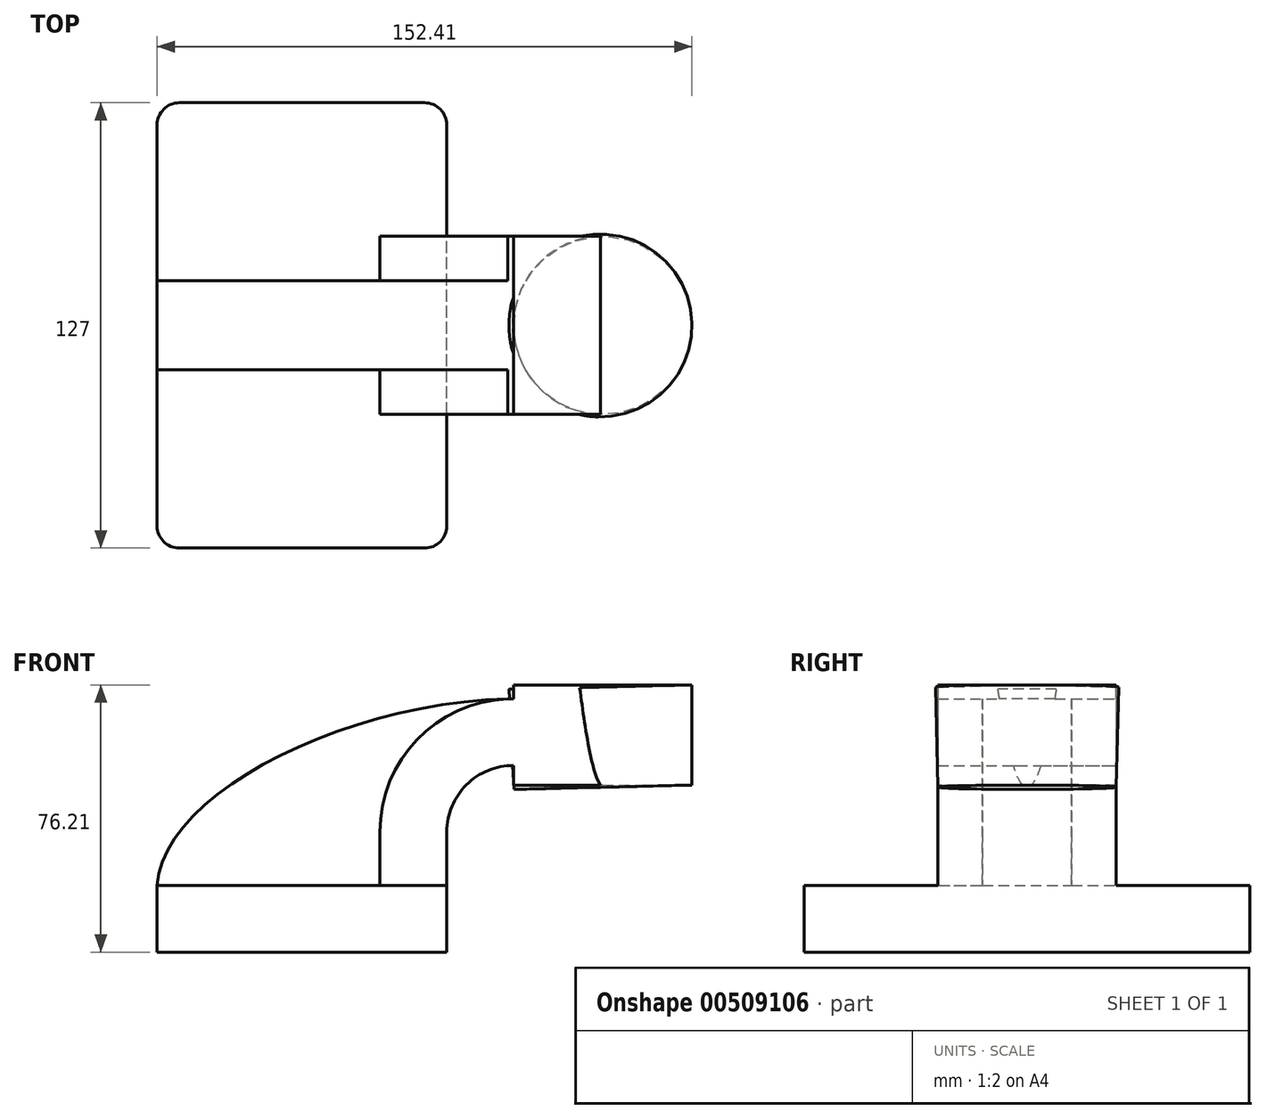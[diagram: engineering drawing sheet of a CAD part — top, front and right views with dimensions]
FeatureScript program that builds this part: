
annotation { "Feature Type Name" : "Feature", "Feature Type Description" : "" }
export const myFeature = defineFeature(function(context is Context, id is Id, definition is map)
    precondition{}
    {
        {
            var Q0;
            Q0=qCreatedBy(makeId("Front.planeOp"),FACE);
            var sketch = newSketch(context, id + "F0", { "sketchPlane" : qUnion([Q0])});
            skLineSegment(sketch, "E0.bottom", {"start": v(-41.28, 9.52) * mm, "end": v(41.28, 9.53) * mm});
            skLineSegment(sketch, "E0.top", {"start": v(-41.28, -9.53) * mm, "end": v(41.28, -9.53) * mm});
            skLineSegment(sketch, "E0.left", {"start": v(-41.28, 9.52) * mm, "end": v(-41.28, -9.53) * mm});
            skLineSegment(sketch, "E0.right", {"start": v(41.28, 9.53) * mm, "end": v(41.28, -9.52) * mm});
            skPoint(sketch, "E0.middle", {"position": v(0, 0) * mm});
            skLineSegment(sketch, "E1.bottom", {"start": v(60.32, 38.1) * mm, "end": v(111.12, 38.1) * mm});
            skLineSegment(sketch, "E1.top", {"start": v(60.32, 66.68) * mm, "end": v(111.12, 66.68) * mm});
            skLineSegment(sketch, "E1.left", {"start": v(60.32, 38.1) * mm, "end": v(60.32, 66.68) * mm});
            skLineSegment(sketch, "E1.right", {"start": v(111.12, 38.1) * mm, "end": v(111.12, 66.68) * mm});
            skPoint(sketch, "E1.middle", {"position": v(85.72, 52.39) * mm});
            skPoint(sketch, "E2.endSnap0", {"position": v(85.72, 38.1) * mm});
            skLineSegment(sketch, "E3", {"start": v(41.28, 9.53) * mm, "end": v(41.28, 24.77) * mm});
            skArc(sketch, "E4", {"start": v(41.27, 24.77) * mm, "mid": v(46.86, 38.19) * mm, "end": v(60.32, 43.67) * mm});
            skLineSegment(sketch, "E5", {"start": v(60.32, 43.67) * mm, "end": v(85.72, 43.67) * mm});
            skArc(sketch, "E6.0", {"start": v(22.23, 24.77) * mm, "mid": v(33.4, 51.66) * mm, "end": v(60.32, 62.72) * mm});
            skLineSegment(sketch, "E7", {"start": v(22.23, 24.77) * mm, "end": v(22.23, 9.53) * mm});
            skLineSegment(sketch, "E8", {"start": v(60.32, 62.72) * mm, "end": v(85.03, 62.72) * mm});
            skLineSegment(sketch, "E9", {"start": v(85.72, 38.1) * mm, "end": v(85.03, 66.68) * mm});
            skFitSpline(sketch, "E10", {"points": [v(-41.28, 9.52) * mm, v(60.32, 62.72) * mm], "startDerivative": vector(4.2, 78.01) * mm, "endDerivative": vector(143.8, 1.78) * mm});
            skSolve(sketch);
        }
        {
            var Q0;
            Q0=makeQuery(id+"F0.imprint","IMPRINT",FACE,{"disambiguationData":[TD([[makeQuery(id+"F0.imprint","IMPRINT",EDGE,{"derivedFrom":sQuery(id+"F0.wireOp",EDGE,"E0.top")}),1.0]])]});
            extrude(context, id + "F1", {"entities" : qUnion([Q0]), "endBound" : BoundingType.SYMMETRIC, "depth" : 127 * mm});
        }
        {
            var Q0;
            {var subQ1=sQuery(id+"F0.wireOp",EDGE,"E3");Q0=makeQuery(id+"F0.imprint","IMPRINT",FACE,{"disambiguationData":[TD([[makeQuery(id+"F0.imprint","IMPRINT",EDGE,{"derivedFrom":subQ1}),1.0]])]});}
            var Q1;
            {var subQ0=sQuery(id+"F0.wireOp",EDGE,"E1.left");var subQ1=sQuery(id+"F0.wireOp",EDGE,"E1.top");var subQ2=makeQuery(id+"F0.imprint","INTERSECT",VERTEX,{"derivedFrom":[subQ1,subQ0]});Q1=makeQuery(id+"F0.imprint","IMPRINT",FACE,{"disambiguationData":[TD([[makeQuery(id+"F0.imprint","IMPRINT",EDGE,{"disambiguationData":[TD([[subQ2,-1.0]])],"derivedFrom":subQ1}),-1.0]])]});}
            var Q2;
            {var subQ0=sQuery(id+"F0.wireOp",EDGE,"E1.left");var subQ1=sQuery(id+"F0.wireOp",EDGE,"E1.bottom");var subQ2=makeQuery(id+"F0.imprint","INTERSECT",VERTEX,{"derivedFrom":[subQ1,subQ0]});Q2=makeQuery(id+"F0.imprint","IMPRINT",FACE,{"disambiguationData":[TD([[makeQuery(id+"F0.imprint","IMPRINT",EDGE,{"disambiguationData":[TD([[subQ2,-1.0]])],"derivedFrom":subQ1}),1.0]])]});}
            extrude(context, id + "F2", {"entities" : qUnion([Q0, Q1, Q2]), "operationType" : NewBodyOperationType.ADD, "endBound" : BoundingType.SYMMETRIC, "depth" : 50.8 * mm});
        }
        {
            var Q0;
            {var subQ3=sQuery(id+"F0.wireOp",EDGE,"E7");Q0=makeQuery(id+"F0.imprint","IMPRINT",FACE,{"disambiguationData":[TD([[makeQuery(id+"F0.imprint","IMPRINT",EDGE,{"derivedFrom":subQ3}),-1.0]])]});}
            extrude(context, id + "F3", {"entities" : qUnion([Q0]), "operationType" : NewBodyOperationType.ADD, "endBound" : BoundingType.SYMMETRIC, "depth" : 25.4 * mm});
        }
        {
            var Q0;
            {var subQ4=sQuery(id+"F0.wireOp",EDGE,"E1.right");Q0=makeQuery(id+"F0.imprint","IMPRINT",FACE,{"disambiguationData":[TD([[makeQuery(id+"F0.imprint","IMPRINT",EDGE,{"derivedFrom":subQ4}),1.0]])]});}
            var Q1;
            Q1=sQuery(id+"F0.wireOp",EDGE,"E9");
            revolve(context, id + "F4", {"operationType" : NewBodyOperationType.ADD, "entities" : qUnion([Q0]), "axis" : qUnion([Q1]), "revolveType" : RevolveType.FULL});
        }
        {
            var Q0;
            Q0=makeQuery(id+"F1.opExtrude","CAP_EDGE",EDGE,{"disambiguationData":[OSD([sQuery(id+"F0.wireOp",EDGE,"E0.left")])],"isStart":false});
            var Q1;
            Q1=makeQuery(id+"F1.opExtrude","CAP_EDGE",EDGE,{"disambiguationData":[OSD([sQuery(id+"F0.wireOp",EDGE,"E0.right")])],"isStart":false});
            var Q2;
            Q2=makeQuery(id+"F1.opExtrude","CAP_EDGE",EDGE,{"disambiguationData":[OSD([sQuery(id+"F0.wireOp",EDGE,"E0.left")])],"isStart":true});
            var Q3;
            Q3=makeQuery(id+"F1.opExtrude","CAP_EDGE",EDGE,{"disambiguationData":[OSD([sQuery(id+"F0.wireOp",EDGE,"E0.right")])],"isStart":true});
            fillet(context, id + "F5", {"entities" : qUnion([Q0, Q1, Q2, Q3]), "radius" : 6.35 * mm, "tangentPropagation" : true, "allowEdgeOverflow" : false});
        }
    });
